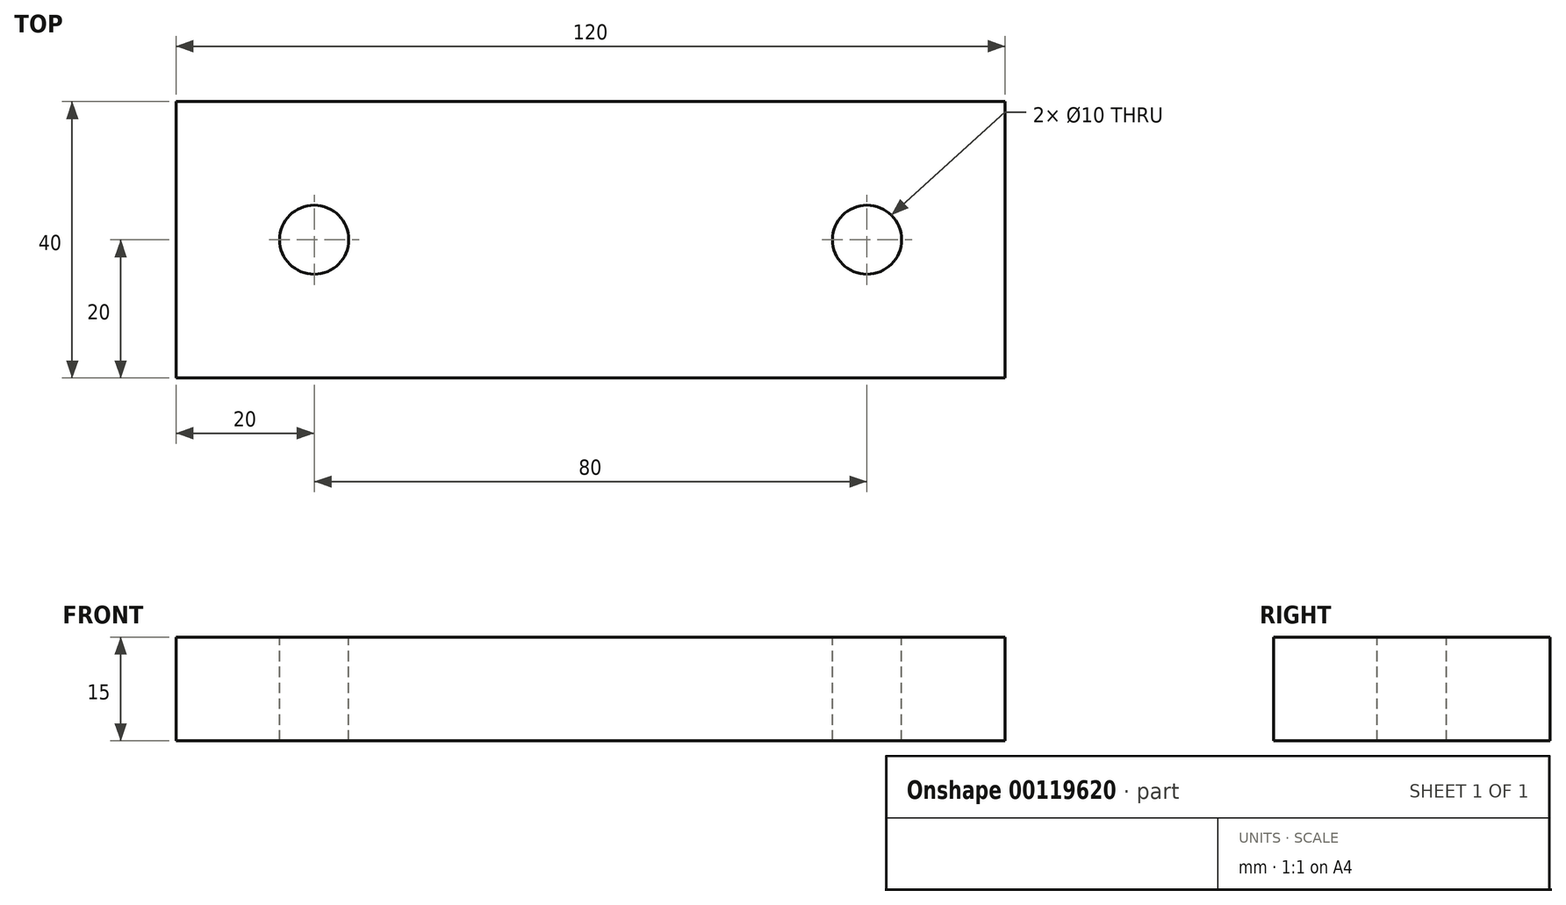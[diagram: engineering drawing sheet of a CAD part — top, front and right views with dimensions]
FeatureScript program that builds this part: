
annotation { "Feature Type Name" : "Feature", "Feature Type Description" : "" }
export const myFeature = defineFeature(function(context is Context, id is Id, definition is map)
    precondition{}
    {
        {
            var Q0;
            Q0=qCreatedBy(makeId("Front.planeOp"),FACE);
            var sketch = newSketch(context, id + "F0", { "sketchPlane" : qUnion([Q0])});
            skLineSegment(sketch, "E0.bottom", {"start": v(0, 0) * mm, "end": v(120, 0) * mm});
            skLineSegment(sketch, "E0.top", {"start": v(0, 15) * mm, "end": v(120, 15) * mm});
            skLineSegment(sketch, "E0.left", {"start": v(0, 0) * mm, "end": v(0, 15) * mm});
            skLineSegment(sketch, "E0.right", {"start": v(120, 0) * mm, "end": v(120, 15) * mm});
            skSolve(sketch);
        }
        {
            var Q0;
            Q0 = qSketchRegion(id + "F0", true);
            extrude(context, id + "F1", {"entities" : qUnion([Q0]), "depth" : 40 * mm});
        }
        {
            var Q0;
            Q0=makeQuery(id+"F1.opExtrude","SWEPT_FACE",FACE,{"disambiguationData":[OSD([sQuery(id+"F0.wireOp",EDGE,"E0.top")])]});
            var sketch = newSketch(context, id + "F2", { "sketchPlane" : qUnion([Q0])});
            skLineSegment(sketch, "E1", {"start": v(0, -20) * mm, "end": v(120, -20) * mm, "construction": true});
            skLineSegment(sketch, "E2", {"start": v(20, -40) * mm, "end": v(20, 0) * mm, "construction": true});
            skLineSegment(sketch, "E3", {"start": v(100, -40) * mm, "end": v(100, 0) * mm, "construction": true});
            skCircle(sketch, "E4", {"center": v(20, -20) * mm, "radius": 5 * mm});
            skCircle(sketch, "E5", {"center": v(100, -20) * mm, "radius": 5 * mm});
            skSolve(sketch);
        }
        {
            var Q0;
            Q0 = qSketchRegion(id + "F2", true);
            extrude(context, id + "F3", {"entities" : qUnion([Q0]), "operationType" : NewBodyOperationType.REMOVE, "endBound" : BoundingType.THROUGH_ALL, "oppositeDirection" : true, "depth" : 25 * mm});
        }
    });
